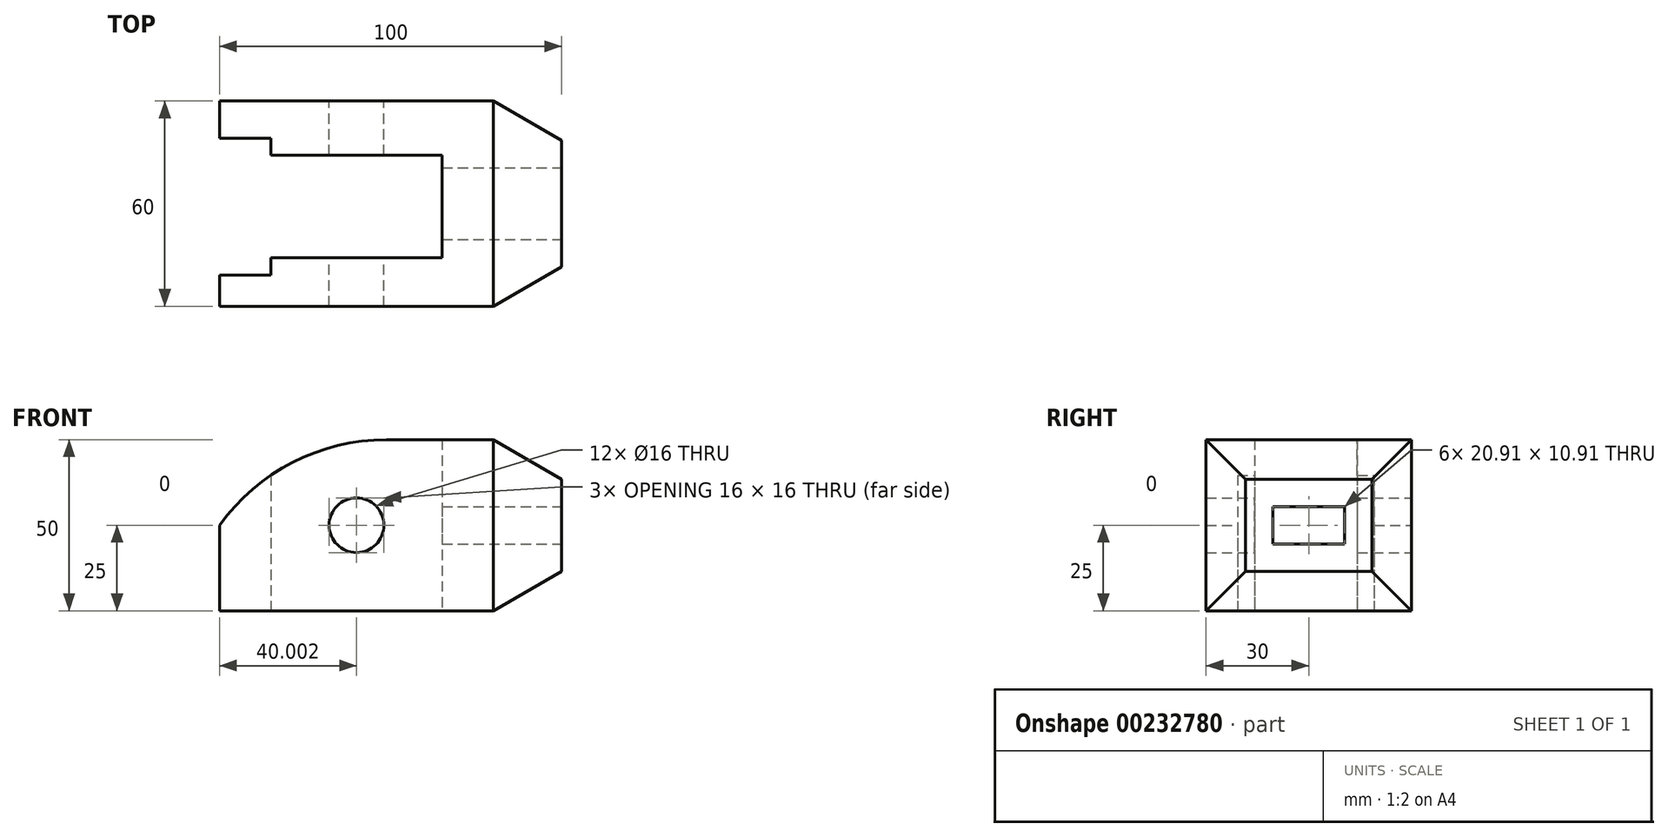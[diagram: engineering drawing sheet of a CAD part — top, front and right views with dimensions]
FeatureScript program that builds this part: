
annotation { "Feature Type Name" : "Feature", "Feature Type Description" : "" }
export const myFeature = defineFeature(function(context is Context, id is Id, definition is map)
    precondition{}
    {
        {
            var Q0;
            Q0=qCreatedBy(makeId("Front.planeOp"),FACE);
            var sketch = newSketch(context, id + "F0", { "sketchPlane" : qUnion([Q0])});
            skLineSegment(sketch, "E0", {"start": v(3.47, 0) * mm, "end": v(-76.53, 0) * mm});
            skLineSegment(sketch, "E1", {"start": v(-76.53, 0) * mm, "end": v(-76.53, 25) * mm});
            skArc(sketch, "E2", {"start": v(-27.8, 50) * mm, "mid": v(-55.18, 43.39) * mm, "end": v(-76.53, 25) * mm});
            skLineSegment(sketch, "E3", {"start": v(-27.8, 50) * mm, "end": v(3.47, 50) * mm});
            skLineSegment(sketch, "E4", {"start": v(3.47, 50) * mm, "end": v(23.47, 38.45) * mm});
            skLineSegment(sketch, "E5", {"start": v(23.47, 38.45) * mm, "end": v(23.47, 11.55) * mm});
            skLineSegment(sketch, "E6", {"start": v(23.47, 11.55) * mm, "end": v(3.47, 0) * mm});
            skCircle(sketch, "E7", {"center": v(-36.53, 25) * mm, "radius": 8 * mm});
            skLineSegment(sketch, "E8", {"start": v(3.47, 50) * mm, "end": v(3.47, 0) * mm});
            skSolve(sketch);
        }
        {
            var Q0;
            Q0=makeQuery(id+"F0.imprint","IMPRINT",FACE,{"disambiguationData":[TD([[makeQuery(id+"F0.imprint","IMPRINT",EDGE,{"derivedFrom":sQuery(id+"F0.wireOp",EDGE,"E0")}),-1.0]])]});
            var Q1;
            Q1=makeQuery(id+"F0.imprint","IMPRINT",FACE,{"disambiguationData":[TD([[makeQuery(id+"F0.imprint","IMPRINT",EDGE,{"derivedFrom":sQuery(id+"F0.wireOp",EDGE,"E4")}),-1.0]])]});
            extrude(context, id + "F1", {"entities" : qUnion([Q0, Q1]), "depth" : 60 * mm});
        }
        {
            var Q0;
            Q0=qCreatedBy(makeId("Top.planeOp"),FACE);
            var sketch = newSketch(context, id + "F2", { "sketchPlane" : qUnion([Q0])});
            skLineSegment(sketch, "E9.0.0", {"start": v(-27.8, 0) * mm, "end": v(-76.53, 0) * mm, "construction": true});
            skLineSegment(sketch, "E9.0.1", {"start": v(-76.53, 0) * mm, "end": v(-76.53, -60) * mm, "construction": true});
            skLineSegment(sketch, "E9.0.2", {"start": v(-76.53, -60) * mm, "end": v(-27.8, -60) * mm, "construction": true});
            skLineSegment(sketch, "E9.0.3", {"start": v(-27.8, -60) * mm, "end": v(-27.8, 0) * mm, "construction": true});
            skLineSegment(sketch, "E10.0.0", {"start": v(3.47, 0) * mm, "end": v(-27.8, 0) * mm, "construction": true});
            skLineSegment(sketch, "E10.0.1", {"start": v(-27.8, 0) * mm, "end": v(-27.8, -60) * mm, "construction": true});
            skLineSegment(sketch, "E10.0.2", {"start": v(-27.8, -60) * mm, "end": v(3.47, -60) * mm, "construction": true});
            skLineSegment(sketch, "E10.0.3", {"start": v(3.47, -60) * mm, "end": v(3.47, 0) * mm, "construction": true});
            skLineSegment(sketch, "E11.0.0", {"start": v(23.47, 0) * mm, "end": v(3.47, 0) * mm, "construction": true});
            skLineSegment(sketch, "E11.0.1", {"start": v(3.47, 0) * mm, "end": v(3.47, -60) * mm, "construction": true});
            skLineSegment(sketch, "E11.0.2", {"start": v(3.47, -60) * mm, "end": v(23.47, -60) * mm, "construction": true});
            skLineSegment(sketch, "E11.0.3", {"start": v(23.47, -60) * mm, "end": v(23.47, 0) * mm, "construction": true});
            skLineSegment(sketch, "E12", {"start": v(3.47, 0) * mm, "end": v(23.47, -11.55) * mm});
            skLineSegment(sketch, "E13", {"start": v(23.47, -48.45) * mm, "end": v(3.47, -60) * mm});
            skLineSegment(sketch, "E14", {"start": v(3.47, -60) * mm, "end": v(23.47, -60) * mm});
            skLineSegment(sketch, "E15", {"start": v(-76.53, -10.83) * mm, "end": v(-61.53, -10.83) * mm});
            skLineSegment(sketch, "E16", {"start": v(-61.53, -10.83) * mm, "end": v(-61.53, -15.83) * mm});
            skLineSegment(sketch, "E17", {"start": v(-61.53, -15.83) * mm, "end": v(-11.53, -15.83) * mm});
            skLineSegment(sketch, "E18", {"start": v(-11.53, -15.83) * mm, "end": v(-11.53, -45.83) * mm});
            skLineSegment(sketch, "E19", {"start": v(-11.53, -45.83) * mm, "end": v(-61.53, -45.83) * mm});
            skLineSegment(sketch, "E20", {"start": v(-61.53, -45.83) * mm, "end": v(-61.53, -50.83) * mm});
            skLineSegment(sketch, "E21", {"start": v(-61.53, -50.83) * mm, "end": v(-76.53, -50.83) * mm});
            skLineSegment(sketch, "E22", {"start": v(-76.53, -50.83) * mm, "end": v(-76.53, -10.83) * mm});
            skLineSegment(sketch, "E23", {"start": v(-76.53, -30) * mm, "end": v(23.47, -30) * mm, "construction": true});
            skLineSegment(sketch, "E24", {"start": v(3.47, 0) * mm, "end": v(23.47, 0) * mm});
            skLineSegment(sketch, "E25", {"start": v(23.47, -11.55) * mm, "end": v(23.47, 0) * mm});
            skLineSegment(sketch, "E26", {"start": v(23.47, -48.45) * mm, "end": v(23.47, -60) * mm});
            skSolve(sketch);
        }
        {
            var Q0;
            Q0=makeQuery(id+"F2.imprint","IMPRINT",FACE,{"disambiguationData":[TD([[makeQuery(id+"F2.imprint","IMPRINT",EDGE,{"derivedFrom":sQuery(id+"F2.wireOp",EDGE,"E15")}),-1.0]])]});
            var Q1;
            Q1=makeQuery(id+"F2.imprint","IMPRINT",FACE,{"disambiguationData":[TD([[makeQuery(id+"F2.imprint","IMPRINT",EDGE,{"derivedFrom":sQuery(id+"F2.wireOp",EDGE,"E12")}),1.0]])]});
            var Q2;
            Q2=makeQuery(id+"F2.imprint","IMPRINT",FACE,{"disambiguationData":[TD([[makeQuery(id+"F2.imprint","IMPRINT",EDGE,{"derivedFrom":sQuery(id+"F2.wireOp",EDGE,"E13")}),1.0]])]});
            extrude(context, id + "F3", {"entities" : qUnion([Q0, Q1, Q2]), "operationType" : NewBodyOperationType.REMOVE, "endBound" : BoundingType.THROUGH_ALL, "oppositeDirection" : true, "depth" : 25 * mm});
        }
        {
            var Q0;
            Q0=makeQuery(id+"F2.imprint","IMPRINT",FACE,{"disambiguationData":[TD([[makeQuery(id+"F2.imprint","IMPRINT",EDGE,{"derivedFrom":sQuery(id+"F2.wireOp",EDGE,"E15")}),-1.0]])]});
            var Q1;
            Q1=makeQuery(id+"F2.imprint","IMPRINT",FACE,{"disambiguationData":[TD([[makeQuery(id+"F2.imprint","IMPRINT",EDGE,{"derivedFrom":sQuery(id+"F2.wireOp",EDGE,"E12")}),1.0]])]});
            var Q2;
            Q2=makeQuery(id+"F2.imprint","IMPRINT",FACE,{"disambiguationData":[TD([[makeQuery(id+"F2.imprint","IMPRINT",EDGE,{"derivedFrom":sQuery(id+"F2.wireOp",EDGE,"E13")}),1.0]])]});
            extrude(context, id + "F4", {"entities" : qUnion([Q0, Q1, Q2]), "operationType" : NewBodyOperationType.REMOVE, "endBound" : BoundingType.THROUGH_ALL, "depth" : 84.3 * mm});
        }
        {
            var Q0;
            Q0=makeQuery(id+"F1.opExtrude","SWEPT_FACE",FACE,{"disambiguationData":[OSD([sQuery(id+"F0.wireOp",EDGE,"E5")])]});
            var sketch = newSketch(context, id + "F5", { "sketchPlane" : qUnion([Q0])});
            skLineSegment(sketch, "E27.0", {"start": v(-40.45, 30.45) * mm, "end": v(-19.55, 30.45) * mm});
            skLineSegment(sketch, "E27.1", {"start": v(-40.45, 30.45) * mm, "end": v(-40.45, 19.55) * mm});
            skLineSegment(sketch, "E27.2", {"start": v(-40.45, 19.55) * mm, "end": v(-19.55, 19.55) * mm});
            skLineSegment(sketch, "E27.3", {"start": v(-19.55, 30.45) * mm, "end": v(-19.55, 19.55) * mm});
            skSolve(sketch);
        }
        {
            var Q0;
            Q0=makeQuery(id+"F5.imprint","IMPRINT",FACE,{"disambiguationData":[TD([[makeQuery(id+"F5.imprint","IMPRINT",EDGE,{"derivedFrom":sQuery(id+"F5.wireOp",EDGE,"E27.0")}),-1.0]])]});
            extrude(context, id + "F6", {"entities" : qUnion([Q0]), "operationType" : NewBodyOperationType.REMOVE, "endBound" : BoundingType.THROUGH_ALL, "oppositeDirection" : true, "depth" : 25 * mm});
        }
    });
